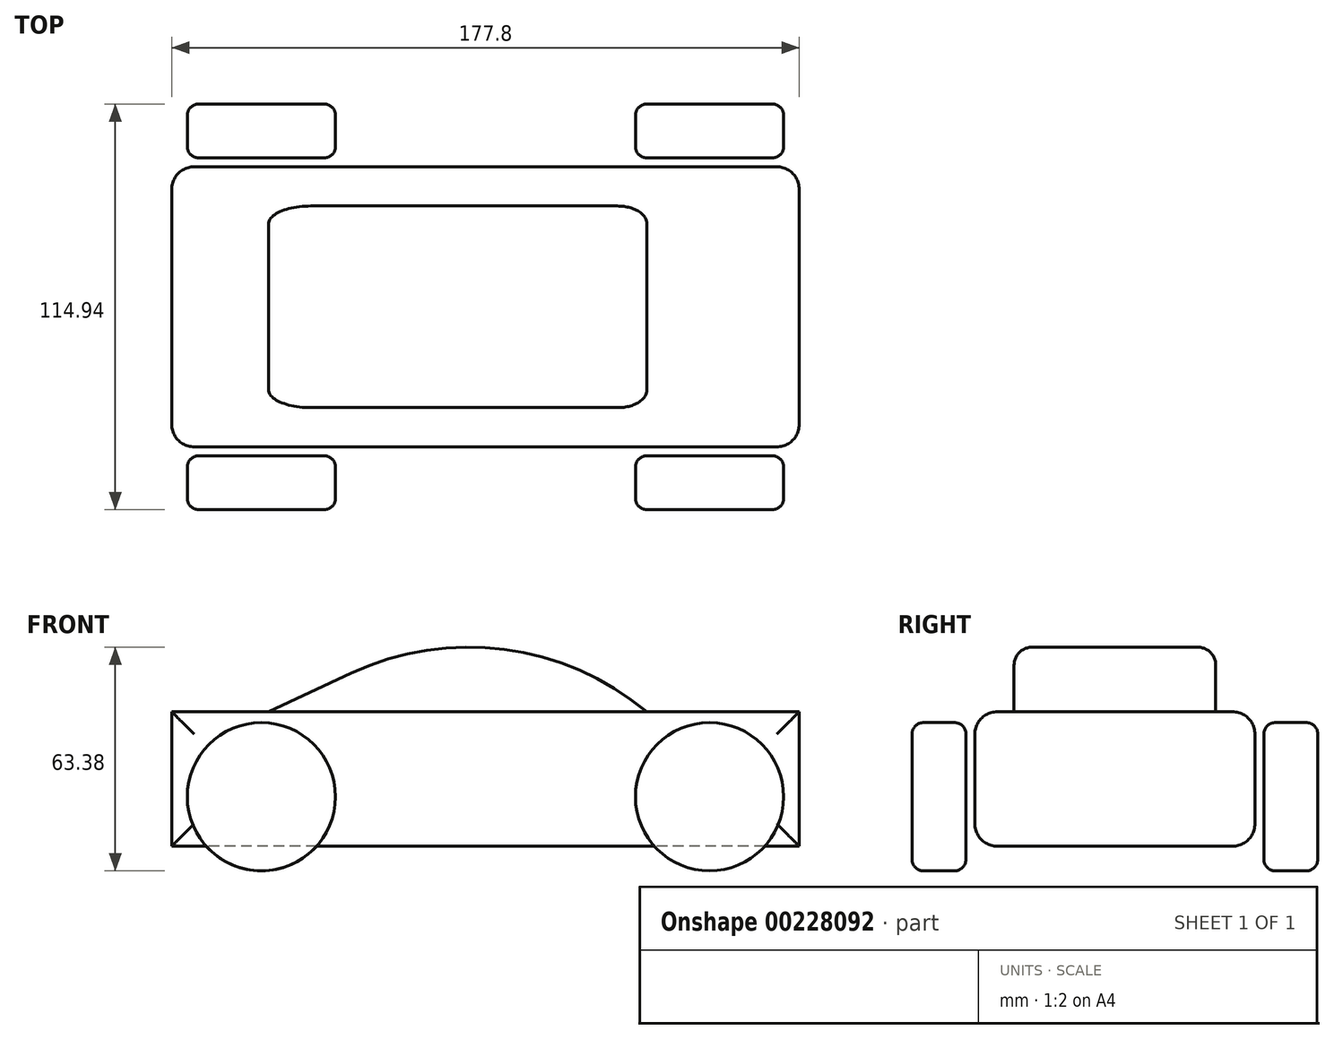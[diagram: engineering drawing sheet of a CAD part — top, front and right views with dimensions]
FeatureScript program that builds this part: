
annotation { "Feature Type Name" : "Feature", "Feature Type Description" : "" }
export const myFeature = defineFeature(function(context is Context, id is Id, definition is map)
    precondition{}
    {
        {
            var Q0;
            Q0=qCreatedBy(makeId("Front.planeOp"),FACE);
            var sketch = newSketch(context, id + "F0", { "sketchPlane" : qUnion([Q0])});
            skLineSegment(sketch, "E0.bottom", {"start": v(88.9, 19.05) * mm, "end": v(-88.9, 19.05) * mm});
            skLineSegment(sketch, "E0.top", {"start": v(88.9, -19.05) * mm, "end": v(-88.9, -19.05) * mm});
            skLineSegment(sketch, "E0.left", {"start": v(88.9, 19.05) * mm, "end": v(88.9, -19.05) * mm});
            skLineSegment(sketch, "E0.right", {"start": v(-88.9, 19.05) * mm, "end": v(-88.9, -19.05) * mm});
            skPoint(sketch, "E0.middle", {"position": v(0, 0) * mm});
            skLineSegment(sketch, "E1", {"start": v(-157.73, -26.03) * mm, "end": v(109.88, -26.03) * mm, "construction": true});
            skCircle(sketch, "E2", {"center": v(63.5, -5.03) * mm, "radius": 21 * mm});
            skSolve(sketch);
        }
        {
            var Q0;
            Q0=qCreatedBy(makeId("Front.planeOp"),FACE);
            var sketch = newSketch(context, id + "F1", { "sketchPlane" : qUnion([Q0])});
            skLineSegment(sketch, "E3.0", {"start": v(-88.9, 19.05) * mm, "end": v(-88.9, -19.05) * mm});
            skLineSegment(sketch, "E3.1", {"start": v(88.9, 19.05) * mm, "end": v(-88.9, 19.05) * mm});
            skLineSegment(sketch, "E3.2", {"start": v(88.9, -19.05) * mm, "end": v(-88.9, -19.05) * mm});
            skLineSegment(sketch, "E3.3", {"start": v(88.9, 19.05) * mm, "end": v(88.9, -19.05) * mm});
            skSolve(sketch);
        }
        {
            var Q0;
            Q0 = qSketchRegion(id + "F1", true);
            extrude(context, id + "F2", {"entities" : qUnion([Q0]), "endBound" : BoundingType.SYMMETRIC, "depth" : 79.38 * mm});
        }
        {
            var Q0;
            Q0=makeQuery(id+"F2.opExtrude","CAP_FACE",FACE,{"disambiguationData":[OSD([sQuery(id+"F1.wireOp",EDGE,"E3.0"),sQuery(id+"F1.wireOp",EDGE,"E3.1"),sQuery(id+"F1.wireOp",EDGE,"E3.2"),sQuery(id+"F1.wireOp",EDGE,"E3.3")])],"isStart":false});
            cPlane(context, id + "F3", {"entities" : qUnion([Q0]), "cplaneType" : CPlaneType.OFFSET, "offset" : 2.54 * mm, "width" : 152.4 * mm, "height" : 152.4 * mm});
        }
        {
            var Q0;
            Q0=qCreatedBy(id+"F3.planeOp",FACE);
            var sketch = newSketch(context, id + "F4", { "sketchPlane" : qUnion([Q0])});
            skCircle(sketch, "E4.0", {"center": v(63.5, -5.03) * mm, "radius": 21 * mm});
            skSolve(sketch);
        }
        {
            var Q0;
            Q0 = qSketchRegion(id + "F4", true);
            extrude(context, id + "F5", {"entities" : qUnion([Q0]), "depth" : 15.24 * mm});
        }
        {
            var Q0;
            Q0=makeQuery(id+"F2.opExtrude","CAP_EDGE",EDGE,{"disambiguationData":[OSD([sQuery(id+"F1.wireOp",EDGE,"E3.1")])],"isStart":false});
            var Q1;
            Q1=makeQuery(id+"F2.opExtrude","CAP_EDGE",EDGE,{"disambiguationData":[OSD([sQuery(id+"F1.wireOp",EDGE,"E3.0")])],"isStart":false});
            var Q2;
            Q2=makeQuery(id+"F2.opExtrude","CAP_EDGE",EDGE,{"disambiguationData":[OSD([sQuery(id+"F1.wireOp",EDGE,"E3.2")])],"isStart":false});
            var Q3;
            Q3=makeQuery(id+"F2.opExtrude","CAP_EDGE",EDGE,{"disambiguationData":[OSD([sQuery(id+"F1.wireOp",EDGE,"E3.3")])],"isStart":false});
            var Q4;
            Q4=makeQuery(id+"F2.opExtrude","CAP_EDGE",EDGE,{"disambiguationData":[OSD([sQuery(id+"F1.wireOp",EDGE,"E3.2")])],"isStart":true});
            var Q5;
            Q5=makeQuery(id+"F2.opExtrude","CAP_EDGE",EDGE,{"disambiguationData":[OSD([sQuery(id+"F1.wireOp",EDGE,"E3.3")])],"isStart":true});
            var Q6;
            Q6=makeQuery(id+"F2.opExtrude","CAP_EDGE",EDGE,{"disambiguationData":[OSD([sQuery(id+"F1.wireOp",EDGE,"E3.0")])],"isStart":true});
            var Q7;
            Q7=makeQuery(id+"F2.opExtrude","CAP_EDGE",EDGE,{"disambiguationData":[OSD([sQuery(id+"F1.wireOp",EDGE,"E3.1")])],"isStart":true});
            fillet(context, id + "F6", {"entities" : qUnion([Q0, Q1, Q2, Q3, Q4, Q5, Q6, Q7]), "radius" : 6.35 * mm, "tangentPropagation" : true, "allowEdgeOverflow" : false});
        }
        {
            var Q0;
            Q0=makeQuery(id+"F5.opExtrude","CAP_EDGE",EDGE,{"disambiguationData":[OSD([sQuery(id+"F4.wireOp",EDGE,"E4.0")])],"isStart":false});
            var Q1;
            Q1=makeQuery(id+"F5.opExtrude","CAP_EDGE",EDGE,{"disambiguationData":[OSD([sQuery(id+"F4.wireOp",EDGE,"E4.0")])],"isStart":true});
            fillet(context, id + "F7", {"entities" : qUnion([Q0, Q1]), "radius" : 3.17 * mm, "tangentPropagation" : true, "allowEdgeOverflow" : false});
        }
        {
            var Q0;
            Q0=makeQuery(id+"F5.opExtrude","SWEPT_BODY",BODY,{"disambiguationData":[OSD([sQuery(id+"F4.wireOp",EDGE,"E4.0")])]});
            var Q1;
            Q1=qCreatedBy(makeId("Front.planeOp"),FACE);
            mirror(context, id + "F8", {"entities" : qUnion([Q0]), "mirrorPlane" : qUnion([Q1])});
        }
        {
            var Q0;
            Q0=makeQuery(id+"F5.opExtrude","SWEPT_BODY",BODY,{"disambiguationData":[OSD([sQuery(id+"F4.wireOp",EDGE,"E4.0")])]});
            var Q1;
            Q1=makeQuery(id+"F8.opPattern","COPY",BODY,{"derivedFrom":makeQuery(id+"F5.opExtrude","SWEPT_BODY",BODY,{"disambiguationData":[OSD([sQuery(id+"F4.wireOp",EDGE,"E4.0")])]}),"instanceName":"1"});
            var Q2;
            Q2=qCreatedBy(makeId("Right.planeOp"),FACE);
            mirror(context, id + "F9", {"entities" : qUnion([Q0, Q1]), "mirrorPlane" : qUnion([Q2])});
        }
        {
            var Q0;
            Q0=qCreatedBy(makeId("Front.planeOp"),FACE);
            var sketch = newSketch(context, id + "F10", { "sketchPlane" : qUnion([Q0])});
            skLineSegment(sketch, "E5", {"start": v(-61.48, 19.05) * mm, "end": v(45.72, 19.05) * mm});
            skLineSegment(sketch, "E6", {"start": v(-61.48, 19.05) * mm, "end": v(-38.1, 29.95) * mm});
            skArc(sketch, "E7", {"start": v(45.72, 19.05) * mm, "mid": v(5.4, 36.68) * mm, "end": v(-38.1, 29.95) * mm});
            skSolve(sketch);
        }
        {
            var Q0;
            Q0 = qSketchRegion(id + "F10", true);
            extrude(context, id + "F11", {"entities" : qUnion([Q0]), "operationType" : NewBodyOperationType.ADD, "endBound" : BoundingType.SYMMETRIC, "depth" : 57.15 * mm});
        }
        {
            var Q0;
            Q0=makeQuery(id+"F11.opExtrude","CAP_EDGE",EDGE,{"disambiguationData":[OSD([sQuery(id+"F10.wireOp",EDGE,"E7")])],"isStart":false});
            var Q1;
            Q1=makeQuery(id+"F11.opExtrude","CAP_EDGE",EDGE,{"disambiguationData":[OSD([sQuery(id+"F10.wireOp",EDGE,"E7")])],"isStart":true});
            fillet(context, id + "F12", {"entities" : qUnion([Q0, Q1]), "radius" : 5.08 * mm, "tangentPropagation" : true, "allowEdgeOverflow" : false});
        }
    });
